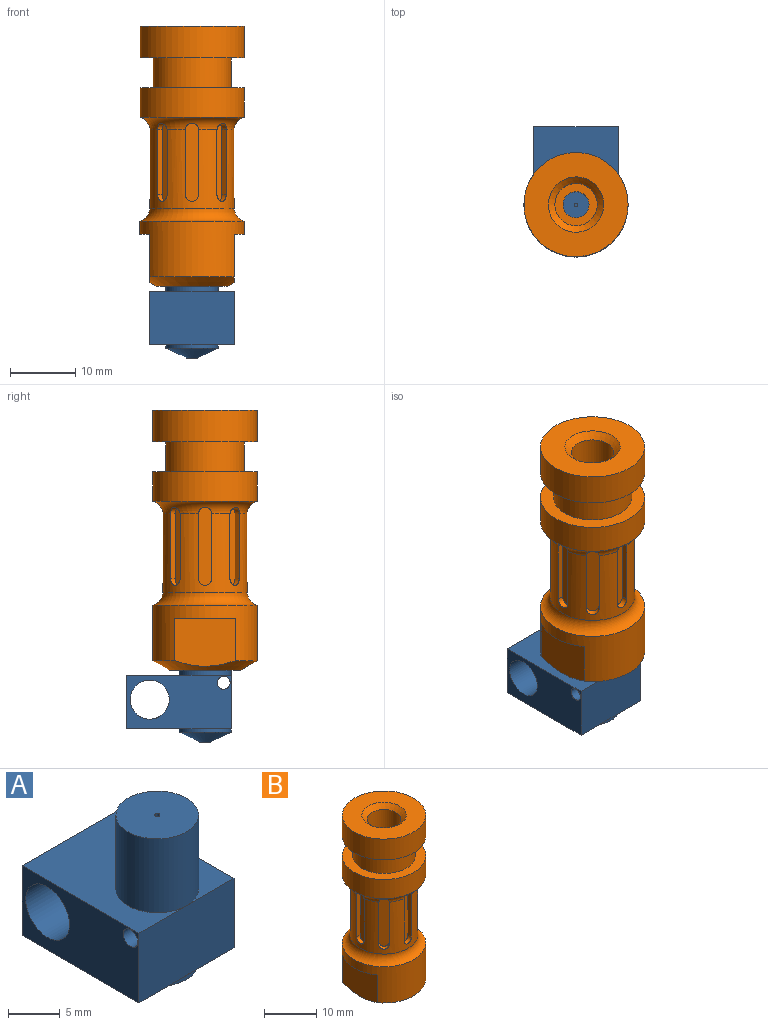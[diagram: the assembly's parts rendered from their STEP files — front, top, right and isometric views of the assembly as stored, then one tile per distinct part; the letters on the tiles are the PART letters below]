
ASSEMBLY  parts=2 mates=1
PART A: 17 faces, bbox 13x16x19 mm
  f0: cylinder r=0.25mm len=8.75mm, axis (0,0,-1), area 13.7mm2, adj f2,f13
  f1: cylinder r=4mm len=8.75mm, axis (0,0,-1), area 219.9mm2, adj f2,f4
  f2: plane 8x8mm, normal (0,0,1), area 50.1mm2, adj f0,f1
  f3: plane 16x13mm, normal (0,0,-1), area 157.7mm2, adj f5,f6,f7,f8,f11
  f4: plane 16x13mm, normal (0,0,1), area 157.7mm2, adj f1,f5,f6,f7,f8
  f5: plane 16x8.25mm, normal (1,0,0), area 100.6mm2, adj f3,f4,f7,f8,f14,f15
  f6: plane 16x8.25mm, normal (-1,0,0), area 100.6mm2, adj f3,f4,f7,f8,f14,f15
  f7: plane 13x8.25mm, normal (0,1,0), area 107.3mm2, adj f3,f4,f5,f6
  f8: plane 13x8.25mm, normal (0,-1,0), area 107.2mm2, adj f3,f4,f5,f6
  f9: cylinder r=0.25mm len=2mm, axis (0,0,-1), area 3.1mm2, adj f10,f12
  f10: plane 1.57x1.57mm, normal (0,0,-1), area 1.7mm2, adj f9,f16
  f11: cylinder r=4mm len=8mm, axis (0,0,-1), area 12.6mm2, adj f3,f16
  f12: plane 0.5x0.5mm, normal (0,0,-1), area 0.2mm2, adj f9
  f13: plane 0.5x0.5mm, normal (0,0,1), area 0.2mm2, adj f0
  f14: cylinder r=3mm len=13mm, axis (-1,0,0), area 245mm2, adj f5,f6
  f15: cylinder r=1mm len=13mm, axis (-1,0,0), area 81.7mm2, adj f5,f6
  f16: cone r=4mm half-angle=65deg, axis (0,0,1), area 53.3mm2, adj f10,f11
PART B: 62 faces, bbox 18.4x18.4x40 mm
  f0: cylinder r=2mm len=24.5mm, axis (0,0,-1), area 307.9mm2, adj f58,f60
  f1: cylinder r=8mm len=16mm, axis (0,0,-1), area 297.8mm2, adj f3,f10,f11,f12,f13,f15
  f2: cylinder r=8mm len=16mm, axis (0,0,-1), area 226.2mm2, adj f9,f16
  f3: cone r=8mm half-angle=60deg, axis (0,0,1), area 104.3mm2, adj f1,f6,f11,f13
  f4: cylinder r=8mm len=16mm, axis (0,0,-1), area 246.3mm2, adj f5,f8
  f5: plane 16x16mm, normal (0,0,1), area 144.3mm2, adj f4,f61
  f6: plane 10.8x10.8mm, normal (0,0,-1), area 41.4mm2, adj f3,f57
  f7: cylinder r=6mm len=12mm, axis (0,0,-1), area 173.4mm2, adj f8,f9
  f8: plane 16x16mm, normal (0,0,-1), area 88mm2, adj f4,f7
  f9: plane 16x16mm, normal (0,0,1), area 88mm2, adj f2,f7
  f10: plane 9.33x1.5mm, normal (0,0,-1), area 9.5mm2, adj f1,f11
  f11: plane 9.33x7.37mm, normal (-1,0,0), area 65.9mm2, adj f1,f3,f10
  f12: plane 9.33x1.5mm, normal (0,0,-1), area 9.5mm2, adj f1,f13
  f13: plane 9.33x7.37mm, normal (1,0,0), area 65.9mm2, adj f1,f3,f12
  f14: cylinder r=6.5mm len=13mm, axis (0,0,-1), area 322mm2, adj f15,f16,f17,f19,f20,f22,f24,f25
  f15: torus R=8.5mm, axis (0,0,-1), area 116.5mm2, adj f1,f14
  f16: torus R=8.5mm, axis (0,0,1), area 103.4mm2, adj f2,f14,f18,f23,f28,f33,f38,f43
  f17: cylinder r=1mm len=2.07mm, axis (0.71,0.71,0), area 2.9mm2, adj f14,f19,f20,f21
  f18: cylinder r=1mm len=2.31mm, axis (0.71,0.71,0), area 3.4mm2, adj f16,f19,f20,f21
  f19: plane 10x0.65mm, normal (-0.71,0.71,0), area 9.2mm2, adj f14,f17,f18,f21
  f20: plane 10x0.65mm, normal (0.71,-0.71,0), area 9.2mm2, adj f14,f17,f18,f21
  f21: plane 12x1.41mm, normal (0.71,0.71,0), area 23.1mm2, adj f17,f18,f19,f20
  f22: cylinder r=1mm len=2mm, axis (0,-1,0), area 2.9mm2, adj f14,f24,f25,f26
  f23: cylinder r=1mm len=2mm, axis (0,-1,0), area 3.4mm2, adj f16,f24,f25,f26
  f24: plane 10x0.92mm, normal (1,0,0), area 9.2mm2, adj f14,f22,f23,f26
  f25: plane 10x0.92mm, normal (-1,0,0), area 9.2mm2, adj f14,f22,f23,f26
  f26: plane 12x2mm, normal (0,-1,0), area 23.1mm2, adj f22,f23,f24,f25
  f27: cylinder r=1mm len=2.07mm, axis (0.71,-0.71,0), area 2.9mm2, adj f14,f29,f30,f31
  f28: cylinder r=1mm len=2.31mm, axis (0.71,-0.71,0), area 3.4mm2, adj f16,f29,f30,f31
  f29: plane 10x0.65mm, normal (0.71,0.71,0), area 9.2mm2, adj f14,f27,f28,f31
  f30: plane 10x0.65mm, normal (-0.71,-0.71,0), area 9.2mm2, adj f14,f27,f28,f31
  f31: plane 12x1.41mm, normal (0.71,-0.71,0), area 23.1mm2, adj f27,f28,f29,f30
  f32: cylinder r=1mm len=2mm, axis (1,0,0), area 2.9mm2, adj f14,f34,f35,f36
  f33: cylinder r=1mm len=2mm, axis (1,0,0), area 3.4mm2, adj f16,f34,f35,f36
  f34: plane 10x0.92mm, normal (0,1,0), area 9.2mm2, adj f14,f32,f33,f36
  f35: plane 10x0.92mm, normal (0,-1,0), area 9.2mm2, adj f14,f32,f33,f36
  f36: plane 12x2mm, normal (1,0,0), area 23.1mm2, adj f32,f33,f34,f35
  f37: cylinder r=1mm len=2mm, axis (0,1,0), area 2.9mm2, adj f14,f39,f40,f41
  f38: cylinder r=1mm len=2mm, axis (0,1,0), area 3.4mm2, adj f16,f39,f40,f41
  f39: plane 10x0.92mm, normal (-1,0,0), area 9.2mm2, adj f14,f37,f38,f41
  f40: plane 10x0.92mm, normal (1,0,0), area 9.2mm2, adj f14,f37,f38,f41
  f41: plane 12x2mm, normal (0,1,0), area 23.1mm2, adj f37,f38,f39,f40
  f42: cylinder r=1mm len=2.07mm, axis (-0.71,0.71,0), area 2.9mm2, adj f14,f44,f45,f46
  f43: cylinder r=1mm len=2.31mm, axis (-0.71,0.71,0), area 3.4mm2, adj f16,f44,f45,f46
  f44: plane 10x0.65mm, normal (-0.71,-0.71,0), area 9.2mm2, adj f14,f42,f43,f46
  f45: plane 10x0.65mm, normal (0.71,0.71,0), area 9.2mm2, adj f14,f42,f43,f46
  f46: plane 12x1.41mm, normal (-0.71,0.71,0), area 23.1mm2, adj f42,f43,f44,f45
  f47: cylinder r=1mm len=2mm, axis (-1,0,0), area 3mm2, adj f14,f49,f50,f51
  f48: cylinder r=1mm len=2mm, axis (-1,0,0), area 3.4mm2, adj f16,f49,f50,f51
  f49: plane 10x0.92mm, normal (0,-1,0), area 9.2mm2, adj f14,f47,f48,f51
  f50: plane 10x0.92mm, normal (0,1,0), area 9.2mm2, adj f14,f47,f48,f51
  f51: plane 12x2mm, normal (-1,0,0), area 23.1mm2, adj f47,f48,f49,f50
  f52: cylinder r=1mm len=2.07mm, axis (-0.71,-0.71,0), area 2.9mm2, adj f14,f54,f55,f56
  f53: cylinder r=1mm len=2.31mm, axis (-0.71,-0.71,0), area 3.4mm2, adj f16,f54,f55,f56
  f54: plane 10x0.65mm, normal (0.71,-0.71,0), area 9.2mm2, adj f14,f52,f53,f56
  f55: plane 10x0.65mm, normal (-0.71,0.71,0), area 9.2mm2, adj f14,f52,f53,f56
  f56: plane 12x1.41mm, normal (-0.71,-0.71,0), area 23.1mm2, adj f52,f53,f54,f55
  f57: cylinder r=4mm len=8mm, axis (0,0,-1), area 201.1mm2, adj f6,f58
  f58: plane 8x8mm, normal (0,0,-1), area 37.7mm2, adj f0,f57
  f59: cylinder r=3.25mm len=6.5mm, axis (0,0,1), area 132.7mm2, adj f60,f61
  f60: plane 6.5x6.5mm, normal (0,0,1), area 20.6mm2, adj f0,f59
  f61: cone r=3.25mm half-angle=45deg, axis (0,0,1), area 33.3mm2, adj f5,f59
PLACE A t=(0.59,-1.01,-10.99)mm
PLACE B t=(0.59,-1.01,0)mm
MATE cylindrical A.f0 <-> B.f0  axis (0,0,-1) through (0.59,-1.01,3.64)mm
